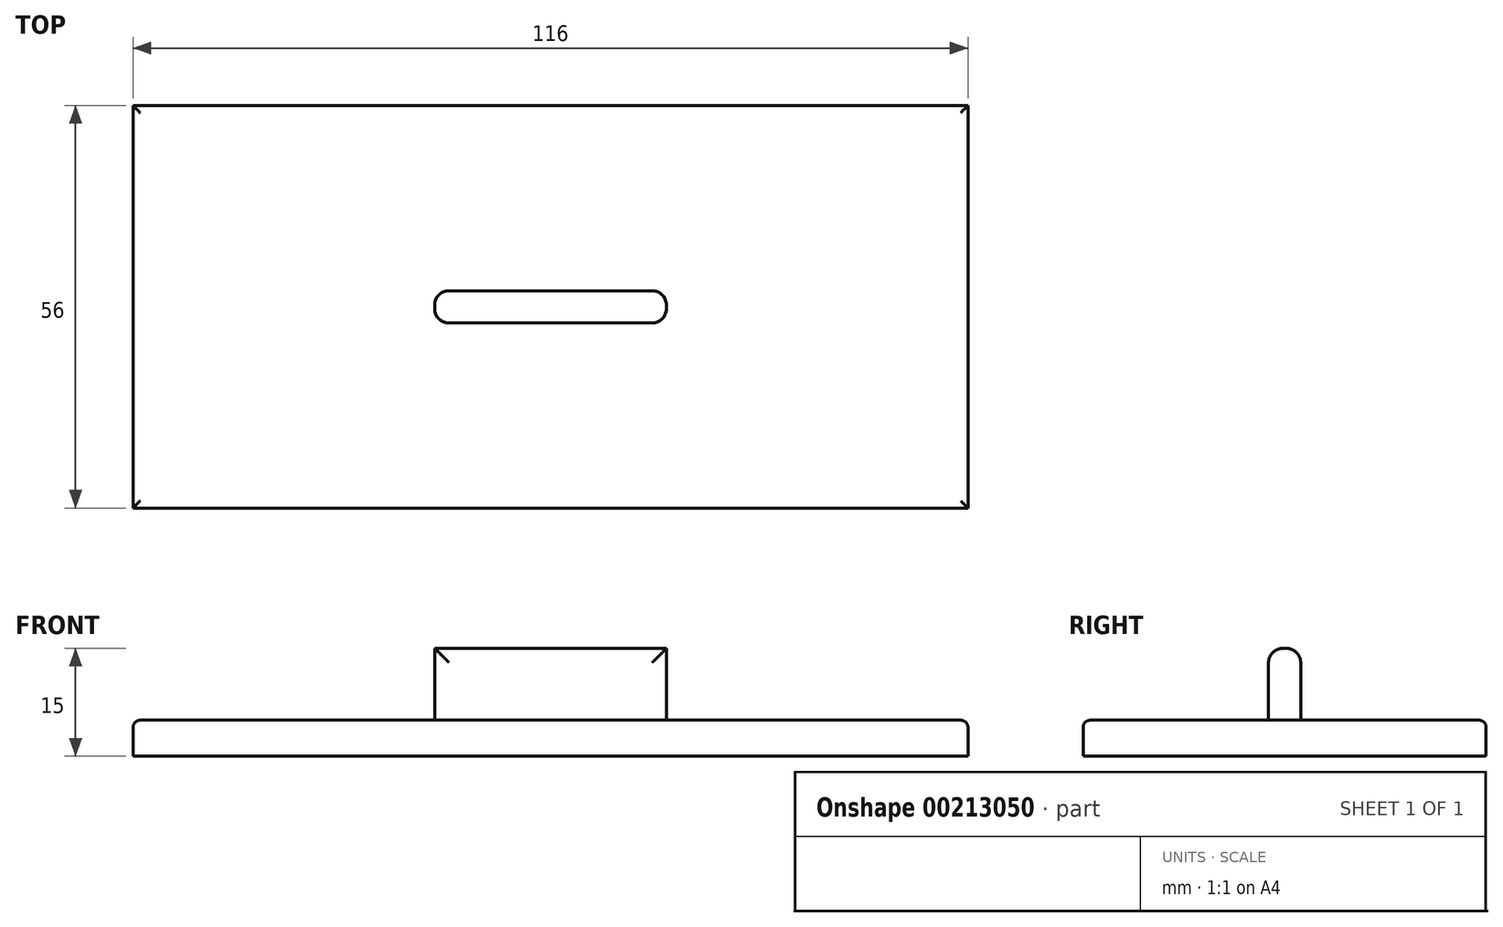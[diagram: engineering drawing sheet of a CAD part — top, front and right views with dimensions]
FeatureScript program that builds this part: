
annotation { "Feature Type Name" : "Feature", "Feature Type Description" : "" }
export const myFeature = defineFeature(function(context is Context, id is Id, definition is map)
    precondition{}
    {
        {
            var Q0;
            Q0=qCreatedBy(makeId("Top.planeOp"),FACE);
            var sketch = newSketch(context, id + "F0", { "sketchPlane" : qUnion([Q0])});
            skLineSegment(sketch, "E0.bottom", {"start": v(58, 28) * mm, "end": v(-58, 28) * mm});
            skLineSegment(sketch, "E0.top", {"start": v(58, -28) * mm, "end": v(-58, -28) * mm});
            skLineSegment(sketch, "E0.left", {"start": v(58, 28) * mm, "end": v(58, -28) * mm});
            skLineSegment(sketch, "E0.right", {"start": v(-58, 28) * mm, "end": v(-58, -28) * mm});
            skPoint(sketch, "E0.middle", {"position": v(0, 0) * mm});
            skSolve(sketch);
        }
        {
            var Q0;
            Q0=makeQuery(id+"F0.imprint","IMPRINT",FACE,{"disambiguationData":[TD([[makeQuery(id+"F0.imprint","IMPRINT",EDGE,{"derivedFrom":sQuery(id+"F0.wireOp",EDGE,"E0.bottom")}),1.0]])]});
            extrude(context, id + "F1", {"entities" : qUnion([Q0]), "depth" : 5 * mm});
        }
        {
            var Q0;
            Q0=makeQuery(id+"F1.opExtrude","CAP_EDGE",EDGE,{"disambiguationData":[OSD([sQuery(id+"F0.wireOp",EDGE,"E0.top")])],"isStart":false});
            var Q1;
            Q1=makeQuery(id+"F1.opExtrude","CAP_EDGE",EDGE,{"disambiguationData":[OSD([sQuery(id+"F0.wireOp",EDGE,"E0.right")])],"isStart":false});
            var Q2;
            Q2=makeQuery(id+"F1.opExtrude","CAP_EDGE",EDGE,{"disambiguationData":[OSD([sQuery(id+"F0.wireOp",EDGE,"E0.bottom")])],"isStart":false});
            var Q3;
            Q3=makeQuery(id+"F1.opExtrude","CAP_EDGE",EDGE,{"disambiguationData":[OSD([sQuery(id+"F0.wireOp",EDGE,"E0.left")])],"isStart":false});
            var Q4;
            Q4=makeQuery(id+"F1.opExtrude","CAP_FACE",FACE,{"disambiguationData":[OSD([sQuery(id+"F0.wireOp",EDGE,"E0.bottom"),sQuery(id+"F0.wireOp",EDGE,"E0.top"),sQuery(id+"F0.wireOp",EDGE,"E0.left"),sQuery(id+"F0.wireOp",EDGE,"E0.right")])],"isStart":false});
            fillet(context, id + "F2", {"entities" : qUnion([Q0, Q1, Q2, Q3, Q4]), "radius" : 1 * mm, "tangentPropagation" : true, "allowEdgeOverflow" : false});
        }
        {
            var Q0;
            Q0=makeQuery(id+"F1.opExtrude","CAP_FACE",FACE,{"disambiguationData":[OSD([sQuery(id+"F0.wireOp",EDGE,"E0.bottom"),sQuery(id+"F0.wireOp",EDGE,"E0.top"),sQuery(id+"F0.wireOp",EDGE,"E0.left"),sQuery(id+"F0.wireOp",EDGE,"E0.right")])],"isStart":false});
            var sketch = newSketch(context, id + "F3", { "sketchPlane" : qUnion([Q0])});
            skLineSegment(sketch, "E1.bottom", {"start": v(16.1, 2.24) * mm, "end": v(-16.1, 2.24) * mm});
            skLineSegment(sketch, "E1.top", {"start": v(16.1, -2.24) * mm, "end": v(-16.1, -2.24) * mm});
            skLineSegment(sketch, "E1.left", {"start": v(16.1, 2.24) * mm, "end": v(16.1, -2.24) * mm});
            skLineSegment(sketch, "E1.right", {"start": v(-16.1, 2.24) * mm, "end": v(-16.1, -2.24) * mm});
            skPoint(sketch, "E1.middle", {"position": v(0, 0) * mm});
            skSolve(sketch);
        }
        {
            var Q0;
            Q0=makeQuery(id+"F3.imprint","IMPRINT",FACE,{"disambiguationData":[TD([[makeQuery(id+"F3.imprint","IMPRINT",EDGE,{"derivedFrom":sQuery(id+"F3.wireOp",EDGE,"E1.bottom")}),1.0]])]});
            extrude(context, id + "F4", {"entities" : qUnion([Q0]), "operationType" : NewBodyOperationType.ADD, "depth" : 10 * mm});
        }
        {
            var Q0;
            Q0=makeQuery(id+"F4.opExtrude","SWEPT_EDGE",EDGE,{"disambiguationData":[OSD([sQuery(id+"F3.wireOp",EDGE,"E1.top"),sQuery(id+"F3.wireOp",EDGE,"E1.right")])]});
            var Q1;
            Q1=makeQuery(id+"F4.opExtrude","SWEPT_EDGE",EDGE,{"disambiguationData":[OSD([sQuery(id+"F3.wireOp",EDGE,"E1.bottom"),sQuery(id+"F3.wireOp",EDGE,"E1.right")])]});
            var Q2;
            Q2=makeQuery(id+"F4.opExtrude","CAP_EDGE",EDGE,{"disambiguationData":[OSD([sQuery(id+"F3.wireOp",EDGE,"E1.top")])],"isStart":false});
            var Q3;
            Q3=makeQuery(id+"F4.opExtrude","CAP_EDGE",EDGE,{"disambiguationData":[OSD([sQuery(id+"F3.wireOp",EDGE,"E1.bottom")])],"isStart":false});
            var Q4;
            Q4=makeQuery(id+"F4.opExtrude","SWEPT_EDGE",EDGE,{"disambiguationData":[OSD([sQuery(id+"F3.wireOp",EDGE,"E1.top"),sQuery(id+"F3.wireOp",EDGE,"E1.left")])]});
            var Q5;
            Q5=makeQuery(id+"F4.opExtrude","SWEPT_EDGE",EDGE,{"disambiguationData":[OSD([sQuery(id+"F3.wireOp",EDGE,"E1.bottom"),sQuery(id+"F3.wireOp",EDGE,"E1.left")])]});
            var Q6;
            Q6=makeQuery(id+"F4.opExtrude","CAP_EDGE",EDGE,{"disambiguationData":[OSD([sQuery(id+"F3.wireOp",EDGE,"E1.top")])],"isStart":true});
            fillet(context, id + "F5", {"entities" : qUnion([Q0, Q1, Q2, Q3, Q4, Q5, Q6]), "radius" : 2 * mm, "tangentPropagation" : true, "allowEdgeOverflow" : false});
        }
    });
